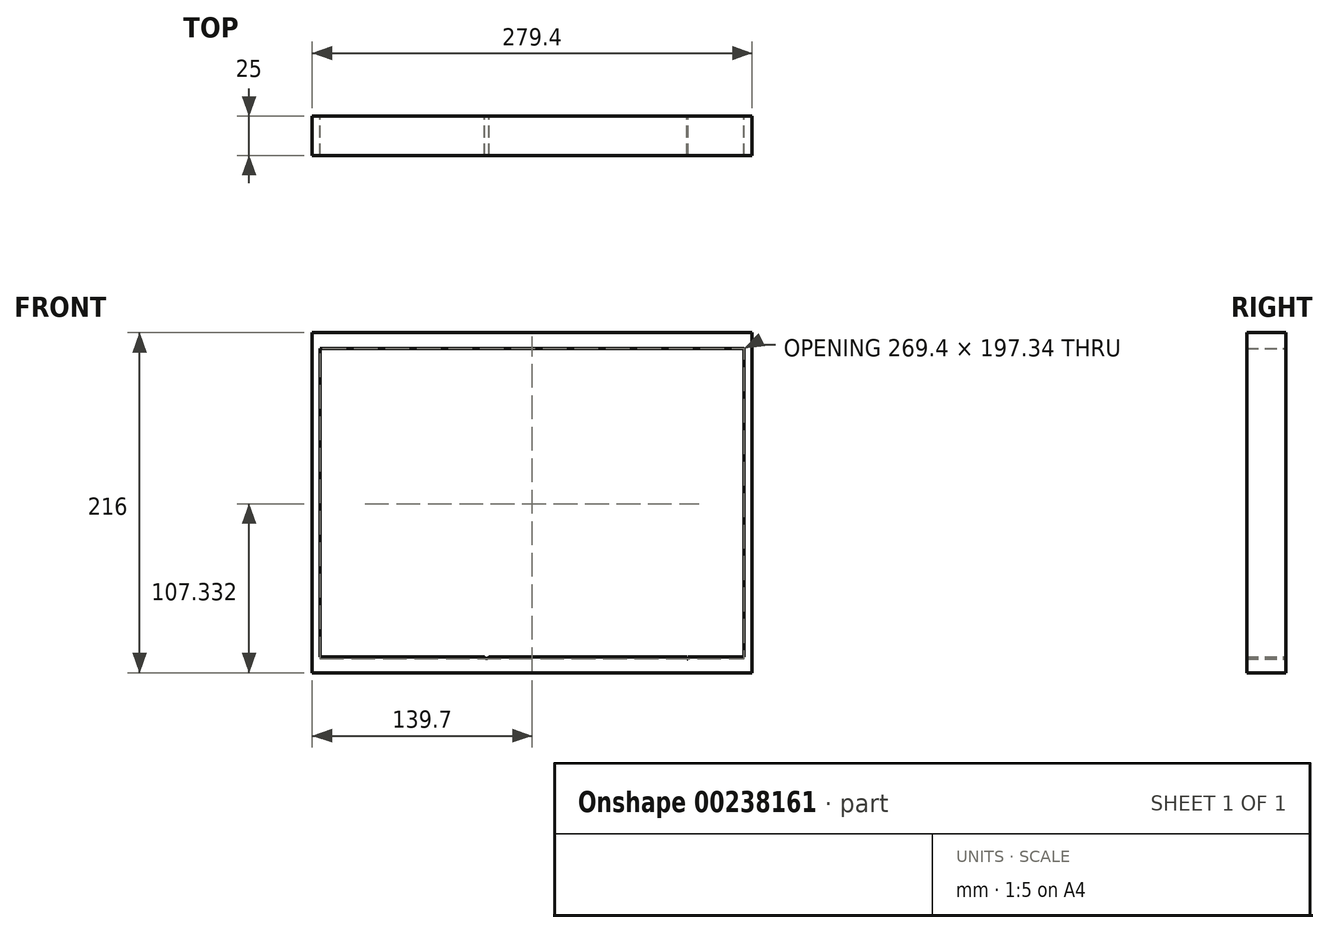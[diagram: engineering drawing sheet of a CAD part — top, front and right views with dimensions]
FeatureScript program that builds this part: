
annotation { "Feature Type Name" : "Feature", "Feature Type Description" : "" }
export const myFeature = defineFeature(function(context is Context, id is Id, definition is map)
    precondition{}
    {
        {
            var Q0;
            Q0=qCreatedBy(makeId("Front.planeOp"),FACE);
            var sketch = newSketch(context, id + "F0", { "sketchPlane" : qUnion([Q0])});
            skLineSegment(sketch, "E0.bottom", {"start": v(0, 0) * mm, "end": v(279.4, 0) * mm});
            skLineSegment(sketch, "E0.top", {"start": v(0, 216) * mm, "end": v(279.4, 216) * mm});
            skLineSegment(sketch, "E0.left", {"start": v(0, 0) * mm, "end": v(0, 216) * mm});
            skLineSegment(sketch, "E0.right", {"start": v(279.4, 0) * mm, "end": v(279.4, 216) * mm});
            skLineSegment(sketch, "E1.bottom", {"start": v(5, 10) * mm, "end": v(274.4, 10) * mm});
            skLineSegment(sketch, "E1.top", {"start": v(5, 206) * mm, "end": v(274.4, 206) * mm});
            skLineSegment(sketch, "E1.left", {"start": v(5, 10) * mm, "end": v(5, 206) * mm});
            skLineSegment(sketch, "E1.right", {"start": v(274.4, 10) * mm, "end": v(274.4, 206) * mm});
            skLineSegment(sketch, "E2", {"start": v(274.4, 40) * mm, "end": v(66.4, 40) * mm});
            skLineSegment(sketch, "E3", {"start": v(220.4, 40) * mm, "end": v(220.4, 10) * mm});
            skLineSegment(sketch, "E4", {"start": v(220.4, 20) * mm, "end": v(274.4, 20) * mm});
            skLineSegment(sketch, "E5", {"start": v(247.4, 20) * mm, "end": v(247.4, 40) * mm});
            skText(sketch, "E6", { "text": "Cliente:", "fontName": "OpenSans-Regular.ttf"});
            skLineSegment(sketch, "E7", {"start": v(135.4, 40) * mm, "end": v(135.4, 10) * mm});
            skLineSegment(sketch, "E8", {"start": v(102.4, 40) * mm, "end": v(102.4, 10) * mm});
            skLineSegment(sketch, "E9", {"start": v(66.4, 40) * mm, "end": v(66.4, 10) * mm});
            skLineSegment(sketch, "E10", {"start": v(135.4, 31) * mm, "end": v(220.4, 31) * mm});
            skLineSegment(sketch, "E11", {"start": v(193.4, 31) * mm, "end": v(193.4, 10) * mm});
            skLineSegment(sketch, "E12", {"start": v(135.4, 20.5) * mm, "end": v(193.4, 20.5) * mm});
            skLineSegment(sketch, "E13", {"start": v(193.4, 24) * mm, "end": v(220.4, 24) * mm});
            skLineSegment(sketch, "E14", {"start": v(102.4, 32) * mm, "end": v(66.4, 32) * mm});
            skText(sketch, "E15", { "text": "Material:", "fontName": "OpenSans-Regular.ttf"});
            skText(sketch, "E16", { "text": "Sistema:", "fontName": "OpenSans-Regular.ttf"});
            skText(sketch, "E17", { "text": "EngineerINC S. A. de C. V.", "fontName": "OpenSans-Regular.ttf"});
            skText(sketch, "E18", { "text": "Pieza:", "fontName": "OpenSans-Regular.ttf"});
            skText(sketch, "E19", { "text": "Compañia", "fontName": "OpenSans-Regular.ttf"});
            skLineSegment(sketch, "E20", {"start": v(193.4, 17) * mm, "end": v(220.4, 17) * mm});
            skText(sketch, "E21", { "text": "Acotaciones:", "fontName": "OpenSans-Regular.ttf"});
            skText(sketch, "E22", { "text": "Fecha:", "fontName": "OpenSans-Regular.ttf"});
            skText(sketch, "E23", { "text": "Diseño:", "fontName": "OpenSans-Regular.ttf"});
            skLineSegment(sketch, "E24", {"start": v(102.4, 30) * mm, "end": v(135.4, 30) * mm});
            skLineSegment(sketch, "E25", {"start": v(102.4, 20) * mm, "end": v(135.4, 20) * mm});
            skText(sketch, "E26", { "text": "Elaboro:", "fontName": "OpenSans-Regular.ttf"});
            skText(sketch, "E27", { "text": "Aprobó:", "fontName": "OpenSans-Regular.ttf"});
            skPoint(sketch, "E27.firstSnap0", {"position": v(102.9, 28) * mm});
            skText(sketch, "E28", { "text": "Orión G. H.", "fontName": "OpenSans-Regular.ttf"});
            skText(sketch, "E29", { "text": "EngineerINC", "fontName": "OpenSans-Regular.ttf"});
            skText(sketch, "E30", { "text": "EngineerINC", "fontName": "OpenSans-Regular.ttf"});
            skText(sketch, "E31", { "text": "IMPORTANTE", "fontName": "OpenSans-Regular.ttf"});
            skText(sketch, "E32", { "text": "Sistema", "fontName": "OpenSans-Regular.ttf"});
            skText(sketch, "E33", { "text": "Pieza", "fontName": "OpenSans-Regular.ttf"});
            const initialGuessF0  = {"E6": [0.2209, 0.0165, 1, 0, 0.003], "E15": [0.1939, 0.0285, 1, 0, 0.002], "E16": [0.1359, 0.0275, 1, 0, 0.003], "E17": [0.1409, 0.0335, 1, 0, 0.0045], "E18": [0.1359, 0.017, 1, 0, 0.003], "E19": [0.2209, 0.0105, 1, 0, 0.0055], "E21": [0.1939, 0.0215, 1, 0, 0.002], "E22": [0.1939, 0.0145, 1, 0, 0.002], "E23": [0.1029, 0.0365, 1, 0, 0.003], "E26": [0.1029, 0.0265, 1, 0, 0.003], "E27": [0.1029, 0.0165, 1, 0, 0.003], "E28": [0.1029, 0.0305, 1, 0, 0.004], "E29": [0.1029, 0.0205, 1, 0, 0.004], "E30": [0.1029, 0.0105, 1, 0, 0.004], "E31": [0.0669, 0.03396, 1, 0, 0.00404], "E32": [0.1359, 0.021, 1, 0, 0.006], "E33": [0.1359, 0.0105, 1, 0, 0.006]};
            skSetInitialGuess(sketch, initialGuessF0);
            skSolve(sketch);
        }
        {
            var Q0;
            Q0 = qSketchRegion(id + "F0", true);
            extrude(context, id + "F1", {"entities" : qUnion([Q0]), "depth" : 25 * mm});
        }
    });
